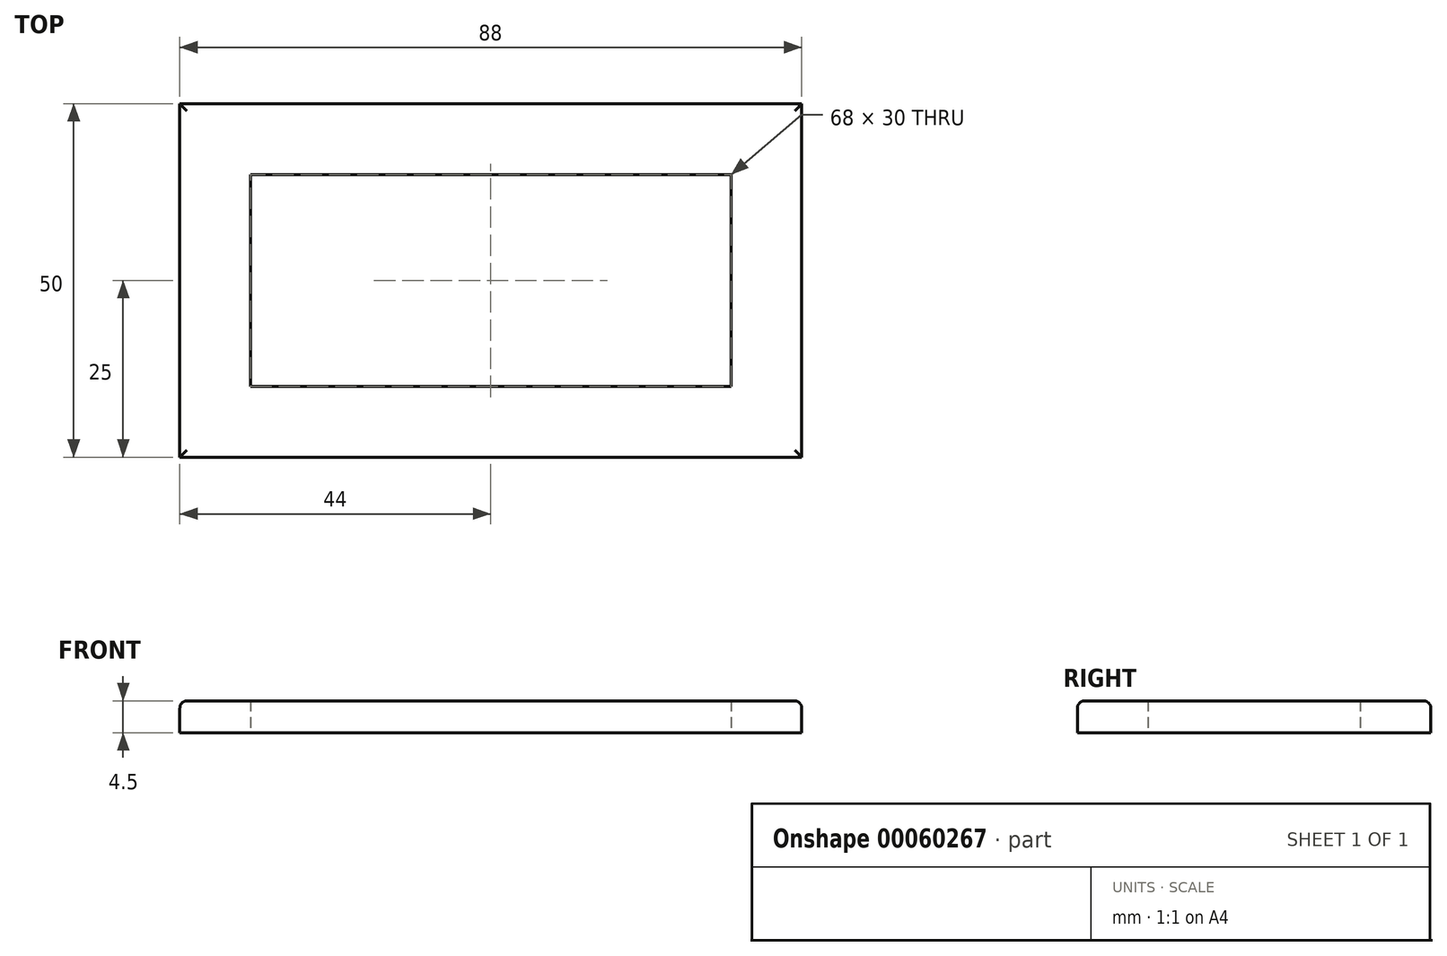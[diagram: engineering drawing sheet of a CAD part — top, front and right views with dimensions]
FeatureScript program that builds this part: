
annotation { "Feature Type Name" : "Feature", "Feature Type Description" : "" }
export const myFeature = defineFeature(function(context is Context, id is Id, definition is map)
    precondition{}
    {
        {
            var Q0;
            Q0=qCreatedBy(makeId("Top.planeOp"),FACE);
            var sketch = newSketch(context, id + "F0", { "sketchPlane" : qUnion([Q0])});
            skLineSegment(sketch, "E0.rect.bottom", {"start": v(-44, 25) * mm, "end": v(44, 25) * mm});
            skLineSegment(sketch, "E0.rect.top", {"start": v(-44, -25) * mm, "end": v(44, -25) * mm});
            skLineSegment(sketch, "E0.rect.left", {"start": v(-44, 25) * mm, "end": v(-44, -25) * mm});
            skLineSegment(sketch, "E0.rect.right", {"start": v(44, 25) * mm, "end": v(44, -25) * mm});
            skPoint(sketch, "E0.rect.middle", {"position": v(0, 0) * mm});
            skLineSegment(sketch, "E1.bottom", {"start": v(34, -15) * mm, "end": v(-34, -15) * mm});
            skLineSegment(sketch, "E1.top", {"start": v(34, 15) * mm, "end": v(-34, 15) * mm});
            skLineSegment(sketch, "E1.left", {"start": v(34, -15) * mm, "end": v(34, 15) * mm});
            skLineSegment(sketch, "E1.right", {"start": v(-34, -15) * mm, "end": v(-34, 15) * mm});
            skSolve(sketch);
        }
        {
            var Q0;
            Q0=makeQuery(id+"F0.imprint","IMPRINT",FACE,{"disambiguationData":[TD([[makeQuery(id+"F0.imprint","IMPRINT",EDGE,{"derivedFrom":sQuery(id+"F0.wireOp",EDGE,"E0.rect.bottom")}),-1.0]])]});
            extrude(context, id + "F1", {"entities" : qUnion([Q0]), "depth" : 4.5 * mm});
        }
        {
            var Q0;
            Q0=makeQuery(id+"F1.opExtrude","CAP_EDGE",EDGE,{"disambiguationData":[OSD([sQuery(id+"F0.wireOp",EDGE,"E0.rect.bottom")])],"isStart":false});
            var Q1;
            Q1=makeQuery(id+"F1.opExtrude","CAP_EDGE",EDGE,{"disambiguationData":[OSD([sQuery(id+"F0.wireOp",EDGE,"E0.rect.right")])],"isStart":false});
            var Q2;
            Q2=makeQuery(id+"F1.opExtrude","CAP_EDGE",EDGE,{"disambiguationData":[OSD([sQuery(id+"F0.wireOp",EDGE,"E0.rect.top")])],"isStart":false});
            var Q3;
            Q3=makeQuery(id+"F1.opExtrude","CAP_EDGE",EDGE,{"disambiguationData":[OSD([sQuery(id+"F0.wireOp",EDGE,"E0.rect.left")])],"isStart":false});
            fillet(context, id + "F2", {"entities" : qUnion([Q0, Q1, Q2, Q3]), "radius" : 1 * mm, "tangentPropagation" : true, "allowEdgeOverflow" : false});
        }
    });
